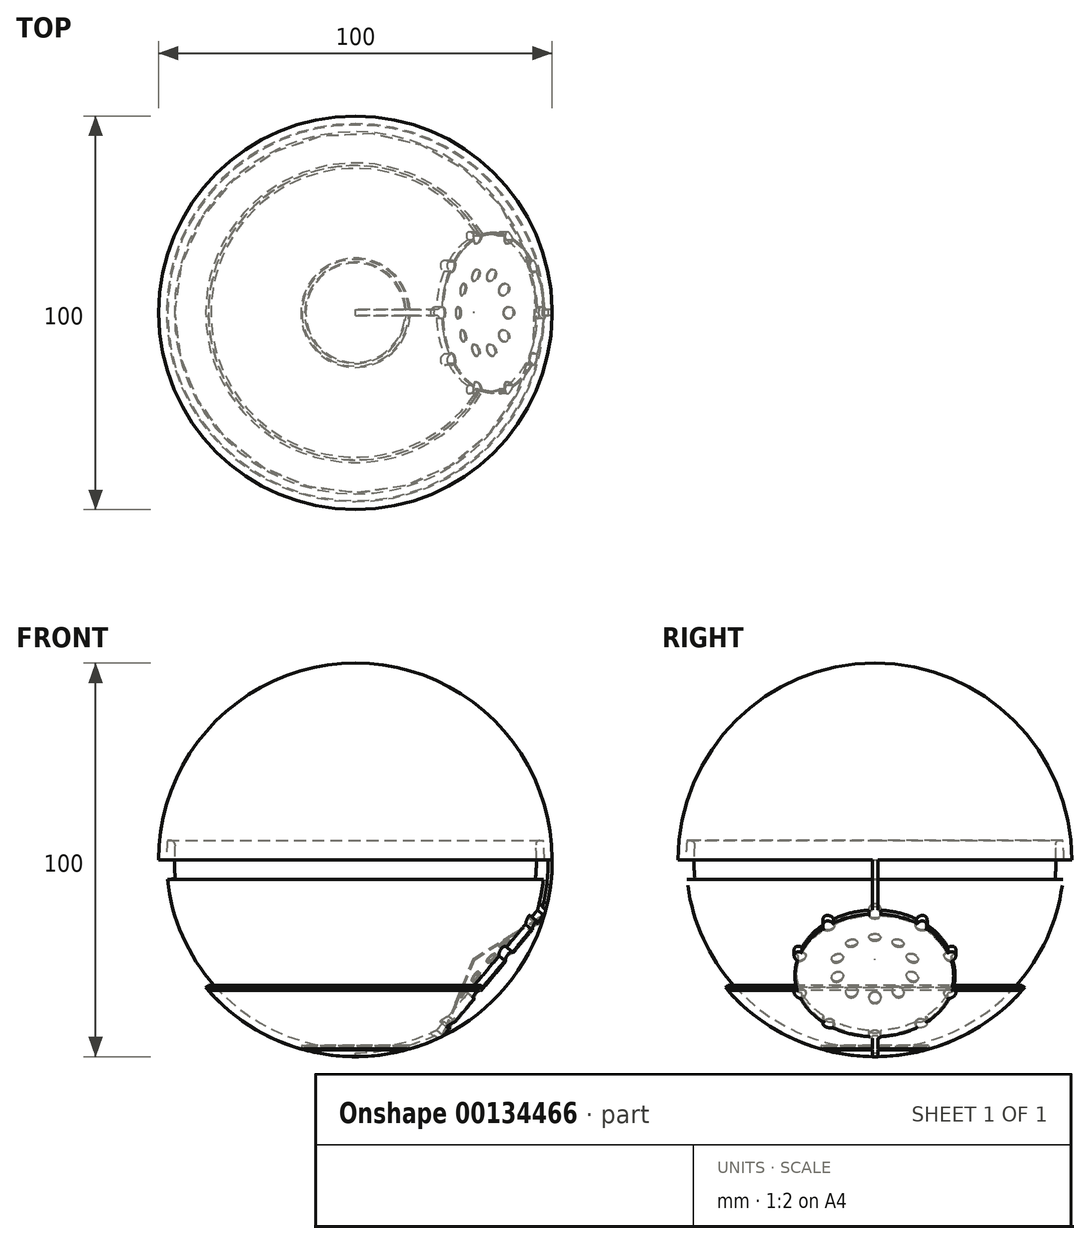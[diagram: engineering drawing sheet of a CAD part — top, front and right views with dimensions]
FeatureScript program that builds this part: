
annotation { "Feature Type Name" : "Feature", "Feature Type Description" : "" }
export const myFeature = defineFeature(function(context is Context, id is Id, definition is map)
    precondition{}
    {
        {
            var Q0;
            Q0=qCreatedBy(makeId("Top.planeOp"),FACE);
            var sketch = newSketch(context, id + "F0", { "sketchPlane" : qUnion([Q0])});
            skArc(sketch, "E0", {"start": v(0, -50) * mm, "mid": v(50, 0) * mm, "end": v(0, 50) * mm});
            skLineSegment(sketch, "E1", {"start": v(0, 50) * mm, "end": v(0, -50) * mm});
            skSolve(sketch);
        }
        {
            var Q0;
            Q0=qSketchRegion(id+"F0",true);
            var Q1;
            Q1=sQuery(id+"F0.wireOp",EDGE,"E1");
            revolve(context, id + "F1", {"entities" : qUnion([Q0]), "axis" : qUnion([Q1]), "revolveType" : RevolveType.ONE_DIRECTION, "oppositeDirection" : true, "angle" : 180 * degree});
        }
        {
            var Q0;
            Q0=makeQuery(id+"F1.opRevolve","CAP_FACE",FACE,{"disambiguationData":[OSD([sQuery(id+"F0.wireOp",EDGE,"E0"),sQuery(id+"F0.wireOp",EDGE,"E1")])],"isStart":true});
            shell(context, id + "F2", {"entities" : qUnion([Q0]), "thickness" : 2 * mm});
        }
        {
            var Q0;
            Q0=qCreatedBy(makeId("Front.planeOp"),FACE);
            var sketch = newSketch(context, id + "F3", { "sketchPlane" : qUnion([Q0])});
            skLineSegment(sketch, "E2", {"start": v(37.35, -31.84) * mm, "end": v(36.7, -32.53) * mm});
            skLineSegment(sketch, "E3", {"start": v(36.7, -32.53) * mm, "end": v(37.6, -33.41) * mm});
            skLineSegment(sketch, "E4", {"start": v(37.6, -33.41) * mm, "end": v(38.3, -32.7) * mm});
            skLineSegment(sketch, "E5", {"start": v(38.3, -32.7) * mm, "end": v(37.35, -31.84) * mm});
            skSolve(sketch);
        }
        {
            var Q0;
            Q0=makeQuery(id+"F3.imprint","IMPRINT",FACE,{"disambiguationData":[TD([[makeQuery(id+"F3.imprint","IMPRINT",EDGE,{"derivedFrom":sQuery(id+"F3.wireOp",EDGE,"E2")}),1.0]])]});
            var Q1;
            Q1=makeQuery(id+"F2.opShell","OFFSET_EDGE",EDGE,{"disambiguationData":[OSD([sQuery(id+"F0.wireOp",EDGE,"E0")])]});
            revolve(context, id + "F4", {"operationType" : NewBodyOperationType.REMOVE, "entities" : qUnion([Q0]), "axis" : qUnion([Q1]), "revolveType" : RevolveType.FULL});
        }
        {
            var Q0;
            Q0=qCreatedBy(makeId("Front.planeOp"),FACE);
            var sketch = newSketch(context, id + "F5", { "sketchPlane" : qUnion([Q0])});
            skLineSegment(sketch, "E6", {"start": v(12.6, -47.49) * mm, "end": v(13.56, -47.15) * mm});
            skLineSegment(sketch, "E7", {"start": v(13.56, -47.15) * mm, "end": v(13.99, -48.38) * mm});
            skLineSegment(sketch, "E8", {"start": v(13.99, -48.38) * mm, "end": v(13.04, -48.7) * mm});
            skLineSegment(sketch, "E9", {"start": v(13.04, -48.7) * mm, "end": v(12.6, -47.49) * mm});
            skLineSegment(sketch, "E10", {"start": v(0, -54.42) * mm, "end": v(0, 0) * mm, "construction": true});
            skSolve(sketch);
        }
        {
            var Q0;
            Q0=makeQuery(id+"F5.imprint","IMPRINT",FACE,{"disambiguationData":[TD([[makeQuery(id+"F5.imprint","IMPRINT",EDGE,{"derivedFrom":sQuery(id+"F5.wireOp",EDGE,"E6")}),-1.0]])]});
            var Q1;
            Q1=sQuery(id+"F5.wireOp",EDGE,"E10");
            revolve(context, id + "F6", {"operationType" : NewBodyOperationType.REMOVE, "entities" : qUnion([Q0]), "axis" : qUnion([Q1]), "revolveType" : RevolveType.FULL, "oppositeDirection" : true});
        }
        {
            var Q0;
            Q0=qCreatedBy(makeId("Top.planeOp"),FACE);
            var sketch = newSketch(context, id + "F7", { "sketchPlane" : qUnion([Q0])});
            skLineSegment(sketch, "E11.bottom", {"start": v(50.69, -0.7) * mm, "end": v(49, -0.7) * mm});
            skLineSegment(sketch, "E11.top", {"start": v(50.69, 0.8) * mm, "end": v(49, 0.8) * mm});
            skLineSegment(sketch, "E11.left", {"start": v(50.69, -0.7) * mm, "end": v(50.69, 0.8) * mm});
            skLineSegment(sketch, "E11.right", {"start": v(49, -0.7) * mm, "end": v(49, 0.8) * mm});
            skPoint(sketch, "E11.middle", {"position": v(49.84, 0.04) * mm});
            skLineSegment(sketch, "E12", {"start": v(0, 27.1) * mm, "end": v(0, -34.95) * mm, "construction": true});
            skSolve(sketch);
        }
        {
            var Q0;
            Q0=makeQuery(id+"F7.imprint","IMPRINT",FACE,{"disambiguationData":[TD([[makeQuery(id+"F7.imprint","IMPRINT",EDGE,{"derivedFrom":sQuery(id+"F7.wireOp",EDGE,"E11.bottom")}),-1.0]])]});
            var Q1;
            Q1=sQuery(id+"F7.wireOp",EDGE,"E12");
            revolve(context, id + "F8", {"operationType" : NewBodyOperationType.REMOVE, "entities" : qUnion([Q0]), "axis" : qUnion([Q1]), "revolveType" : RevolveType.ONE_DIRECTION, "oppositeDirection" : true, "angle" : 90 * degree});
        }
        {
            var Q0;
            Q0=qCreatedBy(makeId("Front.planeOp"),FACE);
            var sketch = newSketch(context, id + "F9", { "sketchPlane" : qUnion([Q0])});
            skArc(sketch, "E13", {"start": v(-47.74, 5) * mm, "mid": v(-48, 0) * mm, "end": v(-47.74, -5) * mm});
            skLineSegment(sketch, "E14", {"start": v(-46.1, -4.83) * mm, "end": v(-47.74, -5) * mm});
            skLineSegment(sketch, "E15", {"start": v(-46.73, 4.9) * mm, "end": v(-47.74, 5) * mm});
            skArc(sketch, "E16", {"start": v(-45.84, 3.82) * mm, "mid": v(-46, -0.3) * mm, "end": v(-45.79, -4.43) * mm});
            skPoint(sketch, "E17.visualSharp", {"position": v(-45.75, -4.8) * mm});
            skArc(sketch, "E17.filletArc", {"start": v(-46.1, -4.83) * mm, "mid": v(-45.87, -4.7) * mm, "end": v(-45.79, -4.43) * mm});
            skPoint(sketch, "E18.visualSharp", {"position": v(-45.75, 4.8) * mm});
            skArc(sketch, "E18.filletArc", {"start": v(-45.84, 3.82) * mm, "mid": v(-46.07, 4.54) * mm, "end": v(-46.73, 4.9) * mm});
            skLineSegment(sketch, "E19", {"start": v(0, -9.44) * mm, "end": v(0, 14.23) * mm, "construction": true});
            skSolve(sketch);
        }
        {
            var Q0;
            Q0 = qSketchRegion(id + "F9", true);
            var Q1;
            Q1=sQuery(id+"F9.wireOp",EDGE,"E19");
            revolve(context, id + "F10", {"operationType" : NewBodyOperationType.ADD, "entities" : qUnion([Q0]), "axis" : qUnion([Q1]), "revolveType" : RevolveType.FULL});
        }
        {
            var Q0;
            Q0=sQuery(id+"F0.wireOp",EDGE,"E1");
            cPlane(context, id + "F11", {"entities" : qUnion([Q0]), "cplaneType" : CPlaneType.LINE_ANGLE, "offset" : 25 * mm, "angle" : 50 * degree, "width" : 150 * mm, "height" : 150 * mm});
        }
        {
            var Q0;
            Q0=qCreatedBy(id+"F11.planeOp",FACE);
            var sketch = newSketch(context, id + "F12", { "sketchPlane" : qUnion([Q0])});
            skCircle(sketch, "E20", {"center": v(0, 0) * mm, "radius": 20 * mm});
            skSolve(sketch);
        }
        {
            var Q0;
            Q0=makeQuery(id+"F12.imprint","IMPRINT",FACE,{"disambiguationData":[TD([[makeQuery(id+"F12.imprint","IMPRINT",EDGE,{"derivedFrom":sQuery(id+"F12.wireOp",EDGE,"E20")}),1.0]])]});
            extrude(context, id + "F13", {"entities" : qUnion([Q0]), "operationType" : NewBodyOperationType.REMOVE, "endBound" : BoundingType.THROUGH_ALL, "depth" : 25 * mm});
        }
        {
            var Q0;
            Q0=qCreatedBy(id+"F11.planeOp",FACE);
            cPlane(context, id + "F14", {"entities" : qUnion([Q0]), "cplaneType" : CPlaneType.OFFSET, "offset" : 46 * mm, "width" : 150 * mm, "height" : 150 * mm});
        }
        {
            var Q0;
            Q0=qCreatedBy(id+"F14.planeOp",FACE);
            var sketch = newSketch(context, id + "F15", { "sketchPlane" : qUnion([Q0])});
            skLineSegment(sketch, "E21", {"start": v(19.44, 0) * mm, "end": v(-23.67, 0) * mm, "construction": true});
            skSolve(sketch);
        }
        {
            var Q0;
            Q0=sQuery(id+"F15.wireOp",EDGE,"E21");
            cPlane(context, id + "F16", {"entities" : qUnion([Q0]), "cplaneType" : CPlaneType.LINE_ANGLE, "offset" : 25 * mm, "angle" : 320 * degree, "width" : 150 * mm, "height" : 150 * mm});
        }
        {
            var Q0;
            Q0=qCreatedBy(id+"F16.planeOp",FACE);
            var sketch = newSketch(context, id + "F17", { "sketchPlane" : qUnion([Q0])});
            skLineSegment(sketch, "E22", {"start": v(39.46, 0) * mm, "end": v(45.84, -20.04) * mm});
            skLineSegment(sketch, "E23", {"start": v(45.84, -20.04) * mm, "end": v(45.67, -20.36) * mm});
            skLineSegment(sketch, "E24", {"start": v(45.67, -20.36) * mm, "end": v(39.05, 0) * mm});
            skLineSegment(sketch, "E25", {"start": v(39.05, 0) * mm, "end": v(39.46, 0) * mm});
            skLineSegment(sketch, "E26", {"start": v(32.5, 0) * mm, "end": v(47.77, 0) * mm, "construction": true});
            skSolve(sketch);
        }
        {
            var Q0;
            Q0 = qSketchRegion(id + "F17", true);
            var Q1;
            Q1=sQuery(id+"F17.wireOp",EDGE,"E26");
            revolve(context, id + "F18", {"operationType" : NewBodyOperationType.ADD, "entities" : qUnion([Q0]), "axis" : qUnion([Q1]), "revolveType" : RevolveType.FULL});
        }
        {
            var Q0;
            Q0=qCreatedBy(id+"F11.planeOp",FACE);
            var sketch = newSketch(context, id + "F19", { "sketchPlane" : qUnion([Q0])});
            skCircle(sketch, "E27", {"center": v(0, 10) * mm, "radius": 1.5 * mm});
            skCircle(sketch, "E28", {"center": v(0, 20.02) * mm, "radius": 1.5 * mm});
            skCircle(sketch, "E29.1.0", {"center": v(-5.88, 8.1) * mm, "radius": 1.5 * mm});
            skCircle(sketch, "E29.1.1", {"center": v(-11.77, 16.2) * mm, "radius": 1.5 * mm});
            skCircle(sketch, "E29.2.0", {"center": v(-9.51, 3.1) * mm, "radius": 1.5 * mm});
            skCircle(sketch, "E29.2.1", {"center": v(-19.04, 6.19) * mm, "radius": 1.5 * mm});
            skCircle(sketch, "E29.3.0", {"center": v(-9.51, -3.1) * mm, "radius": 1.5 * mm});
            skCircle(sketch, "E29.3.1", {"center": v(-19.04, -6.19) * mm, "radius": 1.5 * mm});
            skCircle(sketch, "E29.4.0", {"center": v(-5.88, -8.1) * mm, "radius": 1.5 * mm});
            skCircle(sketch, "E29.4.1", {"center": v(-11.77, -16.2) * mm, "radius": 1.5 * mm});
            skCircle(sketch, "E29.5.0", {"center": v(0, -10) * mm, "radius": 1.5 * mm});
            skCircle(sketch, "E29.5.1", {"center": v(0, -20.02) * mm, "radius": 1.5 * mm});
            skCircle(sketch, "E29.6.0", {"center": v(5.88, -8.1) * mm, "radius": 1.5 * mm});
            skCircle(sketch, "E29.6.1", {"center": v(11.77, -16.2) * mm, "radius": 1.5 * mm});
            skCircle(sketch, "E29.7.0", {"center": v(9.51, -3.1) * mm, "radius": 1.5 * mm});
            skCircle(sketch, "E29.7.1", {"center": v(19.04, -6.19) * mm, "radius": 1.5 * mm});
            skCircle(sketch, "E29.8.0", {"center": v(9.51, 3.1) * mm, "radius": 1.5 * mm});
            skCircle(sketch, "E29.8.1", {"center": v(19.04, 6.19) * mm, "radius": 1.5 * mm});
            skCircle(sketch, "E29.9.0", {"center": v(5.88, 8.1) * mm, "radius": 1.5 * mm});
            skCircle(sketch, "E29.9.1", {"center": v(11.77, 16.2) * mm, "radius": 1.5 * mm});
            skPoint(sketch, "E29.center", {"position": v(0, 0) * mm});
            skSolve(sketch);
        }
        {
            var Q0;
            Q0 = qSketchRegion(id + "F19", true);
            extrude(context, id + "F20", {"entities" : qUnion([Q0]), "operationType" : NewBodyOperationType.REMOVE, "endBound" : BoundingType.THROUGH_ALL, "depth" : 25 * mm});
        }
    });
